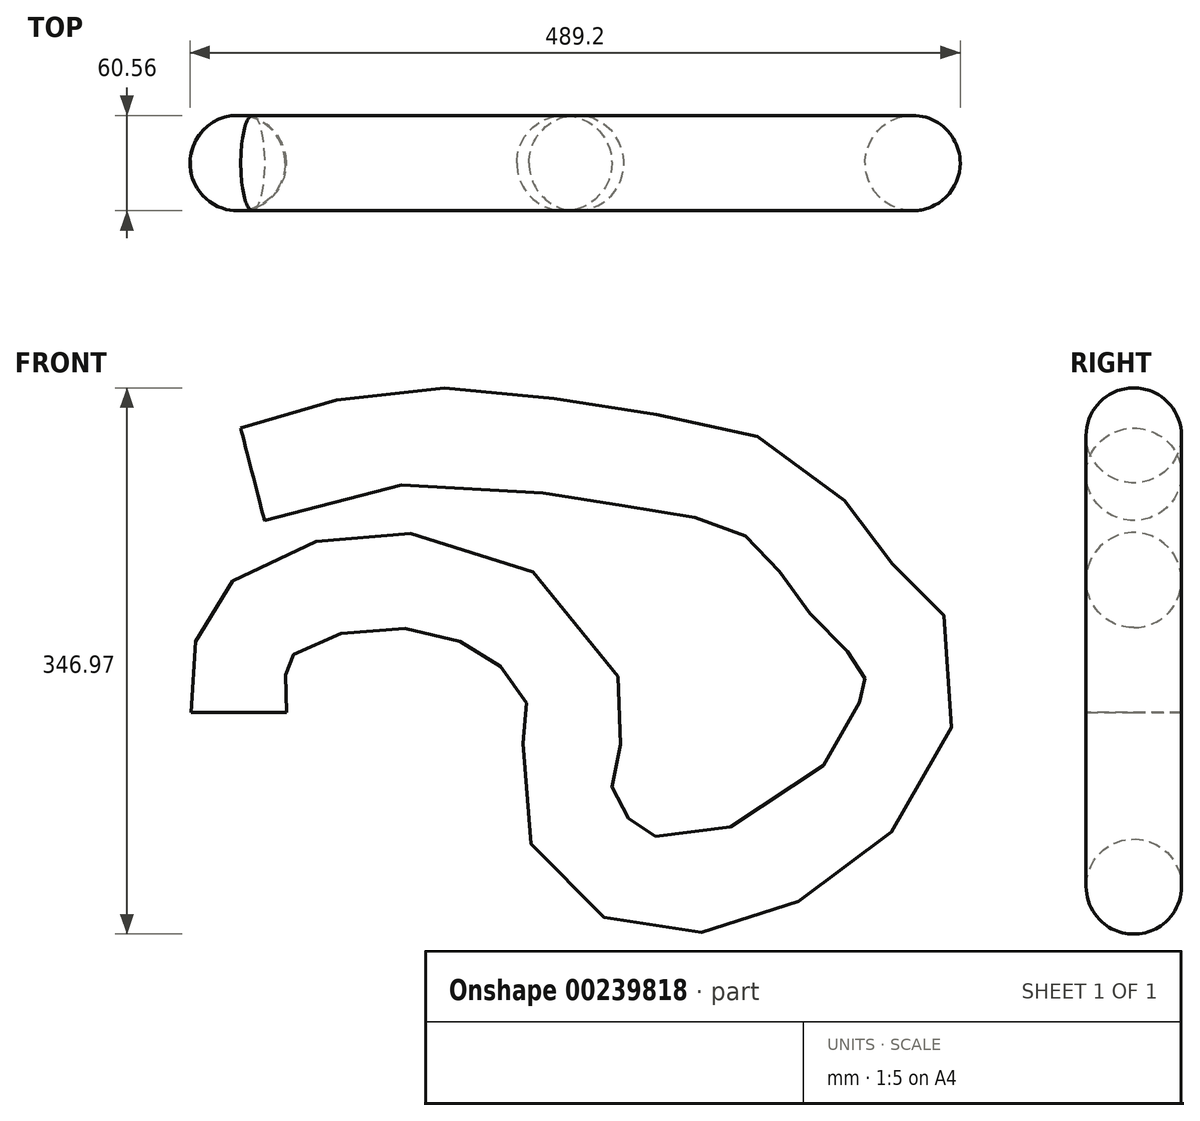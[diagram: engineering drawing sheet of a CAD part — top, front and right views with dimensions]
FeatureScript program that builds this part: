
annotation { "Feature Type Name" : "Feature", "Feature Type Description" : "" }
export const myFeature = defineFeature(function(context is Context, id is Id, definition is map)
    precondition{}
    {
        {
            var Q0;
            Q0=qCreatedBy(makeId("Top.planeOp"),FACE);
            var sketch = newSketch(context, id + "F0", { "sketchPlane" : qUnion([Q0])});
            skCircle(sketch, "E0", {"center": v(0, 0) * mm, "radius": 30.28 * mm});
            skSolve(sketch);
        }
        {
            var Q0;
            Q0=qCreatedBy(makeId("Front.planeOp"),FACE);
            var sketch = newSketch(context, id + "F1", { "sketchPlane" : qUnion([Q0])});
            skFitSpline(sketch, "E1", {"points": [v(0, 0) * mm, v(0, 28.67) * mm, v(15.33, 59.83) * mm, v(79.64, 83.3) * mm, v(145.74, 75.42) * mm, v(189.8, 48.14) * mm, v(214.46, 0) * mm, v(207.12, -52.06) * mm, v(243.84, -102.3) * mm, v(304.68, -106.74) * mm, v(395.32, -52.04) * mm, v(426.48, 36.24) * mm, v(393.35, 73.7) * mm, v(341.9, 134.91) * mm, v(244.72, 161.62) * mm, v(117.1, 175.72) * mm, v(8.8, 151.24) * mm], "startDerivative": vector(-49.52, 697.72) * mm, "endDerivative": vector(-1316.26, -437.37) * mm});
            skSolve(sketch);
        }
        {
            var Q0;
            Q0=makeQuery(id+"F0.imprint","IMPRINT",FACE,{"disambiguationData":[TD([[makeQuery(id+"F0.imprint","IMPRINT",EDGE,{"derivedFrom":sQuery(id+"F0.wireOp",EDGE,"E0")}),1.0]])]});
            var Q1;
            Q1=sQuery(id+"F1.wireOp",EDGE,"E1");
            sweep(context, id + "F2", {"profiles" : qUnion([Q0]), "path" : qUnion([Q1])});
        }
    });
